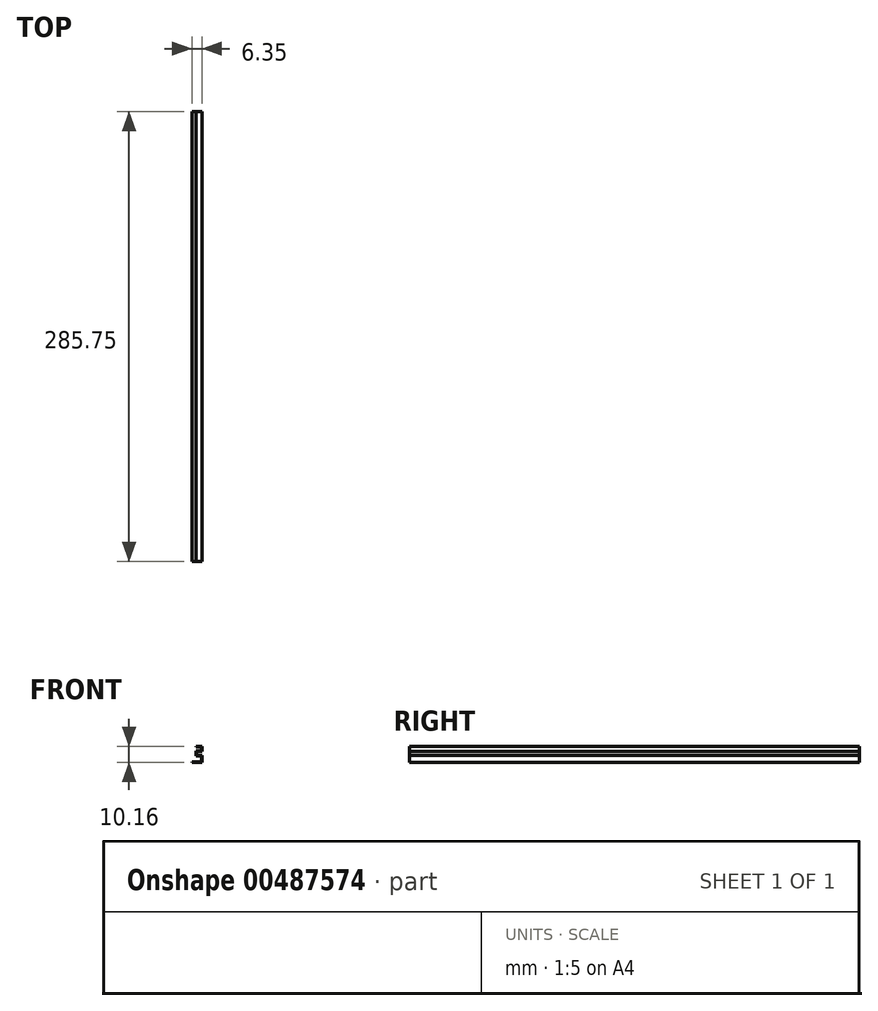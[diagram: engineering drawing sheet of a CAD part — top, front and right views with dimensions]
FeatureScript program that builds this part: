
annotation { "Feature Type Name" : "Feature", "Feature Type Description" : "" }
export const myFeature = defineFeature(function(context is Context, id is Id, definition is map)
    precondition{}
    {
        {
            var Q0;
            Q0=qCreatedBy(makeId("Front.planeOp"),FACE);
            var sketch = newSketch(context, id + "F0", { "sketchPlane" : qUnion([Q0])});
            skLineSegment(sketch, "E0", {"start": v(0, 0) * mm, "end": v(6.35, 0) * mm});
            skLineSegment(sketch, "E1", {"start": v(6.35, 0) * mm, "end": v(6.35, 4.32) * mm});
            skLineSegment(sketch, "E2", {"start": v(6.35, 4.32) * mm, "end": v(2.8, 4.32) * mm});
            skLineSegment(sketch, "E3", {"start": v(2.8, 4.32) * mm, "end": v(2.8, 7.11) * mm});
            skLineSegment(sketch, "E4", {"start": v(2.8, 7.11) * mm, "end": v(6.35, 7.11) * mm});
            skLineSegment(sketch, "E5", {"start": v(6.35, 7.11) * mm, "end": v(6.35, 10.16) * mm});
            skLineSegment(sketch, "E6", {"start": v(6.35, 10.16) * mm, "end": v(2.54, 10.16) * mm});
            skLineSegment(sketch, "E7", {"start": v(2.54, 10.16) * mm, "end": v(2.54, 9.9) * mm});
            skLineSegment(sketch, "E8", {"start": v(2.54, 9.9) * mm, "end": v(6.1, 9.9) * mm});
            skLineSegment(sketch, "E9", {"start": v(6.1, 9.9) * mm, "end": v(6.1, 7.37) * mm});
            skLineSegment(sketch, "E10", {"start": v(6.1, 7.37) * mm, "end": v(2.54, 7.37) * mm});
            skLineSegment(sketch, "E11", {"start": v(2.54, 7.37) * mm, "end": v(2.54, 4.06) * mm});
            skLineSegment(sketch, "E12", {"start": v(2.54, 4.06) * mm, "end": v(6.1, 4.06) * mm});
            skLineSegment(sketch, "E13", {"start": v(6.1, 4.06) * mm, "end": v(6.1, 0.25) * mm});
            skLineSegment(sketch, "E14", {"start": v(6.1, 0.25) * mm, "end": v(0, 0.25) * mm});
            skLineSegment(sketch, "E15", {"start": v(0, 0.25) * mm, "end": v(0, 0) * mm});
            skSolve(sketch);
        }
        {
            var Q0;
            Q0 = qSketchRegion(id + "F0", true);
            extrude(context, id + "F1", {"entities" : qUnion([Q0]), "depth" : 285.75 * mm});
        }
    });
